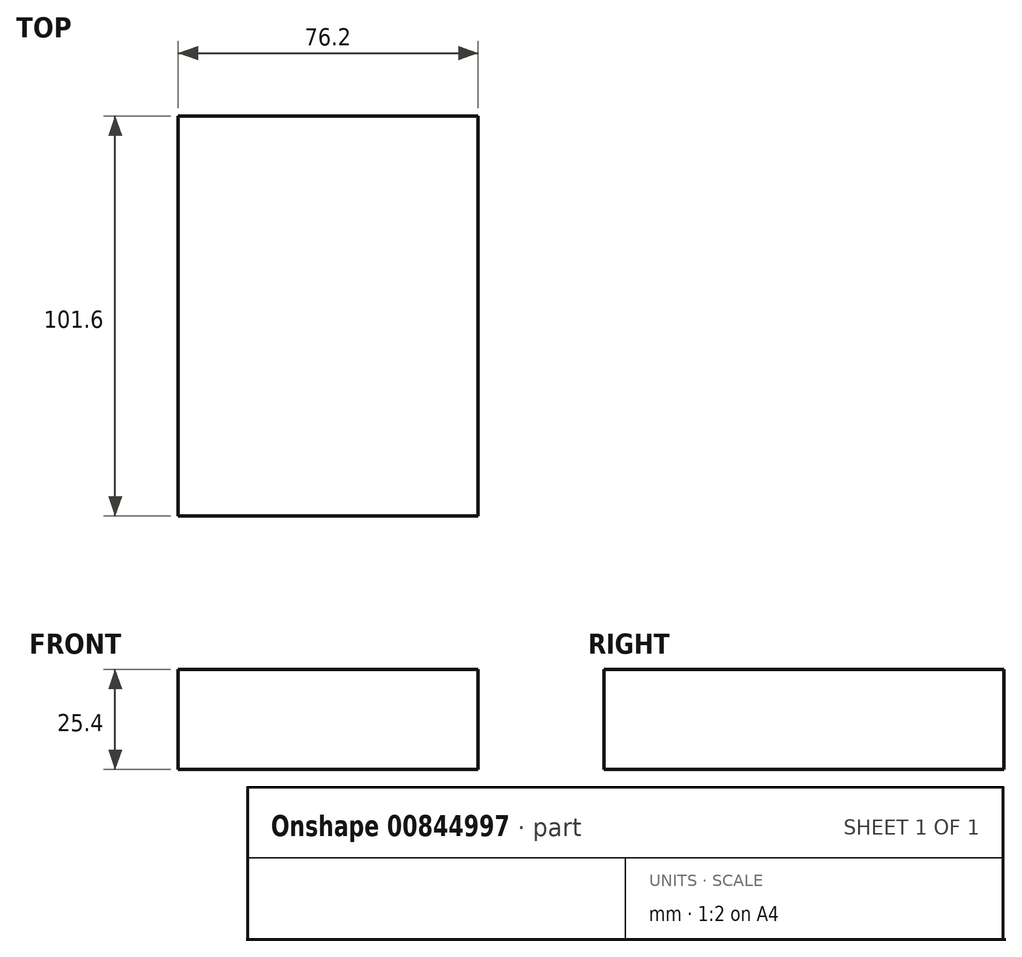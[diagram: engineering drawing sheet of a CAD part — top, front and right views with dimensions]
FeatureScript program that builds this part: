
annotation { "Feature Type Name" : "Feature", "Feature Type Description" : "" }
export const myFeature = defineFeature(function(context is Context, id is Id, definition is map)
    precondition{}
    {
        {
            var Q0;
            Q0=qCreatedBy(makeId("Top.planeOp"),FACE);
            var sketch = newSketch(context, id + "F0", { "sketchPlane" : qUnion([Q0])});
            skLineSegment(sketch, "E0.bottom", {"start": v(0, 0) * mm, "end": v(76.2, 0) * mm});
            skLineSegment(sketch, "E0.top", {"start": v(0, 101.6) * mm, "end": v(76.2, 101.6) * mm});
            skLineSegment(sketch, "E0.left", {"start": v(0, 0) * mm, "end": v(0, 101.6) * mm});
            skLineSegment(sketch, "E0.right", {"start": v(76.2, 0) * mm, "end": v(76.2, 101.6) * mm});
            skSolve(sketch);
        }
        {
            var Q0;
            Q0=makeQuery(id+"F0.imprint","IMPRINT",FACE,{"disambiguationData":[TD([[makeQuery(id+"F0.imprint","IMPRINT",EDGE,{"derivedFrom":sQuery(id+"F0.wireOp",EDGE,"E0.bottom")}),1.0]])]});
            extrude(context, id + "F1", {"entities" : qUnion([Q0]), "depth" : 25.4 * mm, "offsetDistance" : 25.4 * mm});
        }
    });
